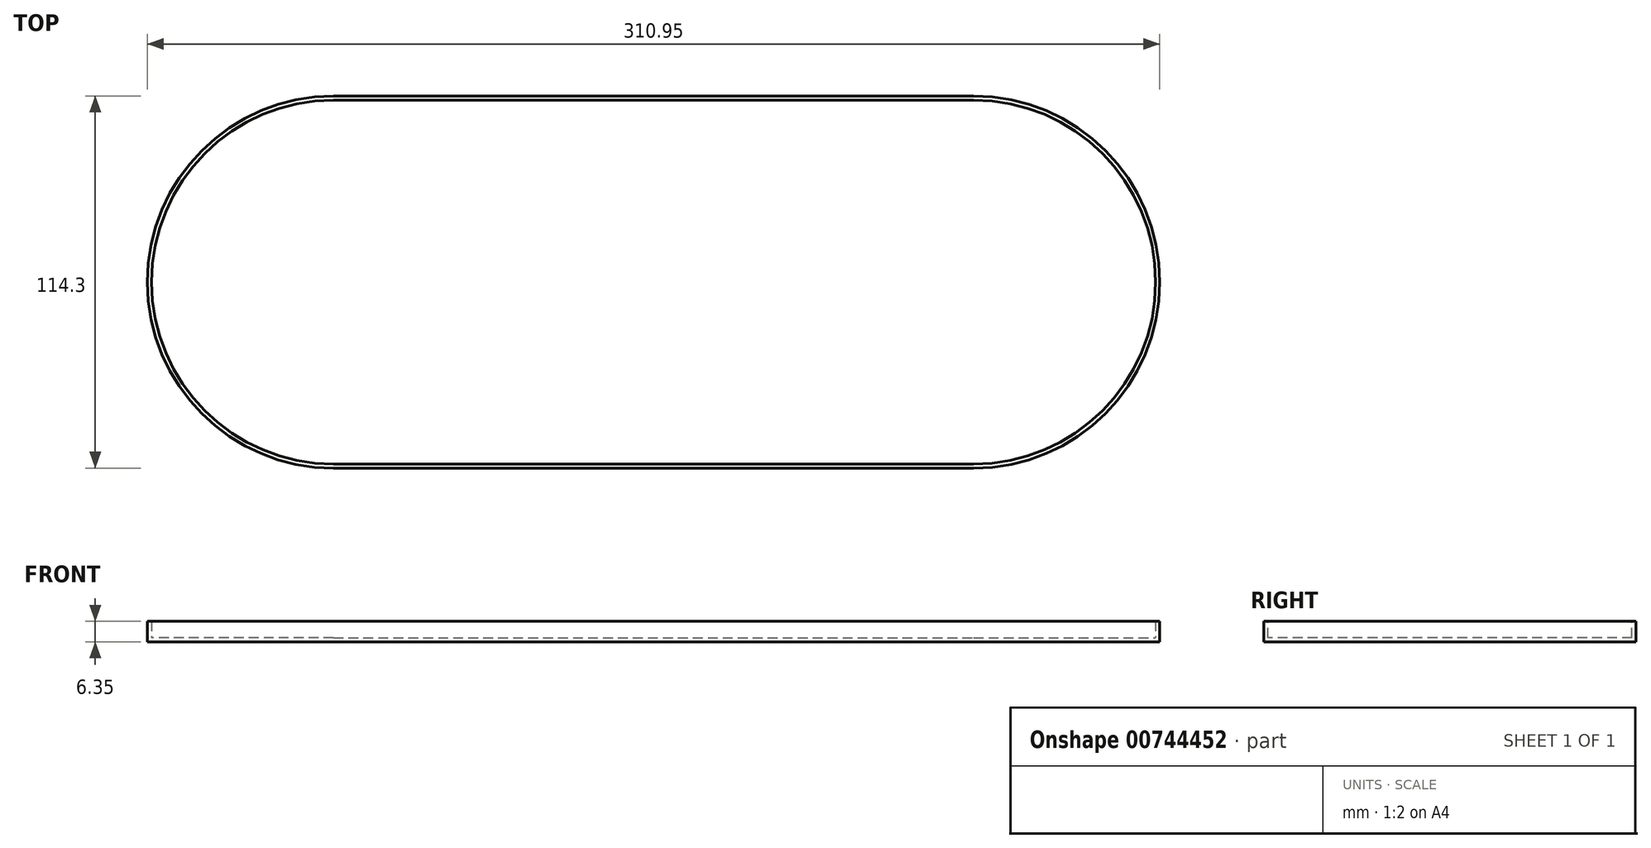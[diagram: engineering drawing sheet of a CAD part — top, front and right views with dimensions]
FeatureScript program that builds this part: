
annotation { "Feature Type Name" : "Feature", "Feature Type Description" : "" }
export const myFeature = defineFeature(function(context is Context, id is Id, definition is map)
    precondition{}
    {
        {
            var Q0;
            Q0=qCreatedBy(makeId("Top.planeOp"),FACE);
            var sketch = newSketch(context, id + "F0", { "sketchPlane" : qUnion([Q0])});
            skArc(sketch, "E0", {"start": v(-196.65, 57.15) * mm, "mid": v(-253.8, 0) * mm, "end": v(-196.65, -57.15) * mm});
            skArc(sketch, "E1", {"start": v(0, -57.15) * mm, "mid": v(57.15, 0) * mm, "end": v(0, 57.15) * mm});
            skLineSegment(sketch, "E2", {"start": v(-196.65, 57.15) * mm, "end": v(0, 57.15) * mm});
            skLineSegment(sketch, "E3", {"start": v(-196.65, -57.15) * mm, "end": v(0, -57.15) * mm});
            skSolve(sketch);
        }
        {
            var Q0;
            Q0=qSketchRegion(id+"F0",true);
            extrude(context, id + "F1", {"entities" : qUnion([Q0]), "depth" : 6.35 * mm});
        }
        {
            var Q0;
            Q0=makeQuery(id+"F1.opExtrude","CAP_FACE",FACE,{"disambiguationData":[OSD([sQuery(id+"F0.wireOp",EDGE,"E0"),sQuery(id+"F0.wireOp",EDGE,"E1"),sQuery(id+"F0.wireOp",EDGE,"E2"),sQuery(id+"F0.wireOp",EDGE,"E3")])],"isStart":false});
            shell(context, id + "F2", {"entities" : qUnion([Q0]), "thickness" : 1.27 * mm});
        }
    });
